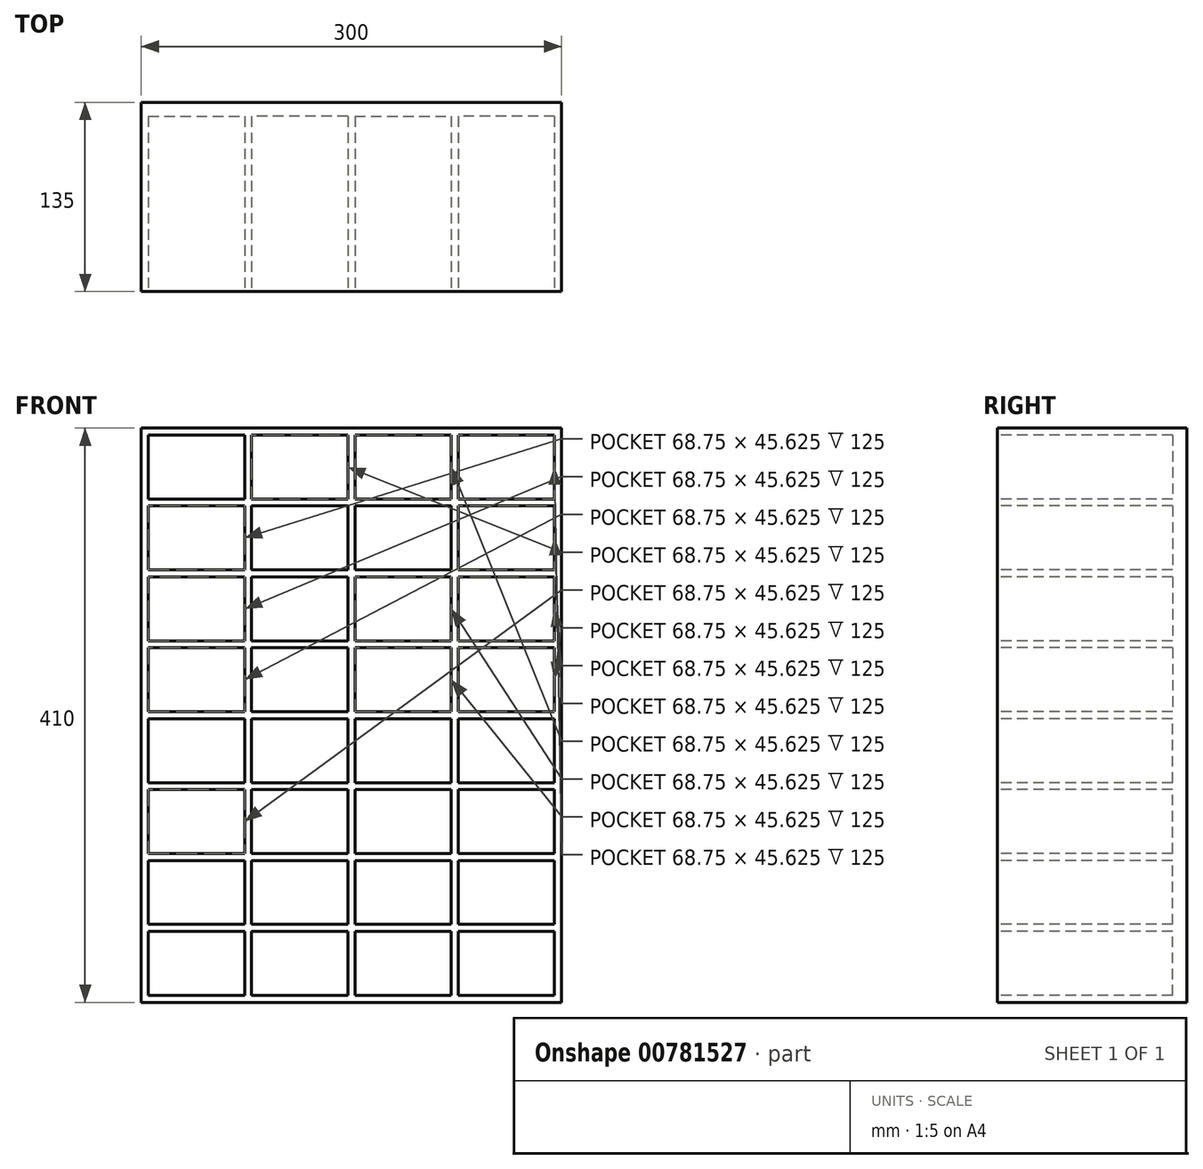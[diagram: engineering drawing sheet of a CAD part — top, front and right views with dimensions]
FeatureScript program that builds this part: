
annotation { "Feature Type Name" : "Feature", "Feature Type Description" : "" }
export const myFeature = defineFeature(function(context is Context, id is Id, definition is map)
    precondition{}
    {
        {
            var Q0;
            Q0=qCreatedBy(makeId("Top.planeOp"),FACE);
            var sketch = newSketch(context, id + "F0", { "sketchPlane" : qUnion([Q0])});
            skLineSegment(sketch, "E0.bottom", {"start": v(0, 0) * mm, "end": v(300, 0) * mm});
            skLineSegment(sketch, "E0.top", {"start": v(0, 135) * mm, "end": v(300, 135) * mm});
            skLineSegment(sketch, "E0.left", {"start": v(0, 0) * mm, "end": v(0, 135) * mm});
            skLineSegment(sketch, "E0.right", {"start": v(300, 0) * mm, "end": v(300, 135) * mm});
            skSolve(sketch);
        }
        {
            var Q0;
            Q0=makeQuery(id+"F0.imprint","IMPRINT",FACE,{"disambiguationData":[TD([[makeQuery(id+"F0.imprint","IMPRINT",EDGE,{"derivedFrom":sQuery(id+"F0.wireOp",EDGE,"E0.bottom")}),1.0]])]});
            extrude(context, id + "F1", {"entities" : qUnion([Q0]), "depth" : 410 * mm, "offsetDistance" : 25 * mm});
        }
        {
            var Q0;
            Q0=makeQuery(id+"F1.opExtrude","SWEPT_FACE",FACE,{"disambiguationData":[OSD([sQuery(id+"F0.wireOp",EDGE,"E0.bottom")])]});
            var sketch = newSketch(context, id + "F2", { "sketchPlane" : qUnion([Q0])});
            skLineSegment(sketch, "E1", {"start": v(0, 205) * mm, "end": v(300, 205) * mm, "construction": true});
            skLineSegment(sketch, "E2.bottom", {"start": v(5, 405) * mm, "end": v(73.75, 405) * mm});
            skLineSegment(sketch, "E2.top", {"start": v(5, 359.38) * mm, "end": v(73.75, 359.38) * mm});
            skLineSegment(sketch, "E2.left", {"start": v(5, 405) * mm, "end": v(5, 359.38) * mm});
            skLineSegment(sketch, "E2.right", {"start": v(73.75, 405) * mm, "end": v(73.75, 359.38) * mm});
            skLineSegment(sketch, "E3.bottom", {"start": v(5, 354.38) * mm, "end": v(73.75, 354.38) * mm});
            skLineSegment(sketch, "E3.top", {"start": v(5, 308.75) * mm, "end": v(73.75, 308.75) * mm});
            skLineSegment(sketch, "E3.left", {"start": v(5, 354.38) * mm, "end": v(5, 308.75) * mm});
            skLineSegment(sketch, "E3.right", {"start": v(73.75, 354.38) * mm, "end": v(73.75, 308.75) * mm});
            skLineSegment(sketch, "E4.bottom", {"start": v(5, 303.75) * mm, "end": v(73.75, 303.75) * mm});
            skLineSegment(sketch, "E4.top", {"start": v(5, 258.12) * mm, "end": v(73.75, 258.12) * mm});
            skLineSegment(sketch, "E4.left", {"start": v(5, 303.75) * mm, "end": v(5, 258.12) * mm});
            skLineSegment(sketch, "E4.right", {"start": v(73.75, 303.75) * mm, "end": v(73.75, 258.13) * mm});
            skLineSegment(sketch, "E5", {"start": v(0, 405) * mm, "end": v(5, 405) * mm});
            skLineSegment(sketch, "E6", {"start": v(5, 359.38) * mm, "end": v(5, 354.38) * mm});
            skLineSegment(sketch, "E7", {"start": v(5, 308.75) * mm, "end": v(5, 303.75) * mm});
            skLineSegment(sketch, "E8.bottom", {"start": v(5, 253.13) * mm, "end": v(73.75, 253.13) * mm});
            skLineSegment(sketch, "E8.top", {"start": v(5, 207.5) * mm, "end": v(73.75, 207.5) * mm});
            skLineSegment(sketch, "E8.left", {"start": v(5, 253.13) * mm, "end": v(5, 207.5) * mm});
            skLineSegment(sketch, "E8.right", {"start": v(73.75, 253.13) * mm, "end": v(73.75, 207.5) * mm});
            skLineSegment(sketch, "E9", {"start": v(5, 258.12) * mm, "end": v(5, 253.13) * mm});
            skLineSegment(sketch, "E10", {"start": v(5, 405) * mm, "end": v(5, 410) * mm});
            skLineSegment(sketch, "E11", {"start": v(76.25, 410) * mm, "end": v(76.25, 205) * mm, "construction": true});
            skLineSegment(sketch, "E12", {"start": v(150, 410) * mm, "end": v(150, 205) * mm, "construction": true});
            skLineSegment(sketch, "E13.MirrorCS", {"start": v(147.5, 405) * mm, "end": v(78.75, 405) * mm});
            skLineSegment(sketch, "E14.MirrorCS", {"start": v(147.5, 405) * mm, "end": v(147.5, 359.38) * mm});
            skLineSegment(sketch, "E15.MirrorCS", {"start": v(78.75, 405) * mm, "end": v(78.75, 359.38) * mm});
            skLineSegment(sketch, "E16.MirrorCS", {"start": v(147.5, 354.38) * mm, "end": v(78.75, 354.38) * mm});
            skLineSegment(sketch, "E17.MirrorCS", {"start": v(78.75, 354.38) * mm, "end": v(78.75, 308.75) * mm});
            skLineSegment(sketch, "E18.MirrorCS", {"start": v(147.5, 359.38) * mm, "end": v(78.75, 359.38) * mm});
            skLineSegment(sketch, "E19.MirrorCS", {"start": v(147.5, 354.38) * mm, "end": v(147.5, 308.75) * mm});
            skLineSegment(sketch, "E20.MirrorCS", {"start": v(147.5, 308.75) * mm, "end": v(78.75, 308.75) * mm});
            skLineSegment(sketch, "E21.MirrorCS", {"start": v(147.5, 303.75) * mm, "end": v(78.75, 303.75) * mm});
            skLineSegment(sketch, "E22.MirrorCS", {"start": v(78.75, 303.75) * mm, "end": v(78.75, 258.13) * mm});
            skLineSegment(sketch, "E23.MirrorCS", {"start": v(147.5, 258.13) * mm, "end": v(78.75, 258.13) * mm});
            skLineSegment(sketch, "E24.MirrorCS", {"start": v(147.5, 303.75) * mm, "end": v(147.5, 258.12) * mm});
            skLineSegment(sketch, "E25.MirrorCS", {"start": v(147.5, 253.13) * mm, "end": v(78.75, 253.13) * mm});
            skLineSegment(sketch, "E26.MirrorCS", {"start": v(78.75, 253.13) * mm, "end": v(78.75, 207.5) * mm});
            skLineSegment(sketch, "E27.MirrorCS", {"start": v(147.5, 207.5) * mm, "end": v(78.75, 207.5) * mm});
            skLineSegment(sketch, "E28.MirrorCS", {"start": v(147.5, 253.13) * mm, "end": v(147.5, 207.5) * mm});
            skLineSegment(sketch, "E29", {"start": v(73.75, 405) * mm, "end": v(78.75, 405) * mm});
            skLineSegment(sketch, "E30.MirrorCS", {"start": v(221.25, 354.38) * mm, "end": v(221.25, 308.75) * mm});
            skLineSegment(sketch, "E31.MirrorCS", {"start": v(152.5, 405) * mm, "end": v(152.5, 359.38) * mm});
            skLineSegment(sketch, "E32.MirrorCS", {"start": v(221.25, 303.75) * mm, "end": v(221.25, 258.13) * mm});
            skLineSegment(sketch, "E33.MirrorCS", {"start": v(152.5, 354.38) * mm, "end": v(152.5, 308.75) * mm});
            skLineSegment(sketch, "E34.MirrorCS", {"start": v(152.5, 253.13) * mm, "end": v(152.5, 207.5) * mm});
            skLineSegment(sketch, "E35.MirrorCS", {"start": v(221.25, 253.13) * mm, "end": v(221.25, 207.5) * mm});
            skLineSegment(sketch, "E36.MirrorCS", {"start": v(152.5, 303.75) * mm, "end": v(152.5, 258.12) * mm});
            skLineSegment(sketch, "E37.MirrorCS", {"start": v(221.25, 405) * mm, "end": v(221.25, 359.38) * mm});
            skLineSegment(sketch, "E38.MirrorCS", {"start": v(152.5, 303.75) * mm, "end": v(221.25, 303.75) * mm});
            skLineSegment(sketch, "E39.MirrorCS", {"start": v(152.5, 258.13) * mm, "end": v(221.25, 258.13) * mm});
            skLineSegment(sketch, "E40.MirrorCS", {"start": v(152.5, 354.38) * mm, "end": v(221.25, 354.38) * mm});
            skLineSegment(sketch, "E41.MirrorCS", {"start": v(152.5, 207.5) * mm, "end": v(221.25, 207.5) * mm});
            skLineSegment(sketch, "E42.MirrorCS", {"start": v(152.5, 359.38) * mm, "end": v(221.25, 359.38) * mm});
            skLineSegment(sketch, "E43.MirrorCS", {"start": v(152.5, 308.75) * mm, "end": v(221.25, 308.75) * mm});
            skLineSegment(sketch, "E44.MirrorCS", {"start": v(152.5, 253.13) * mm, "end": v(221.25, 253.13) * mm});
            skLineSegment(sketch, "E45.MirrorCS", {"start": v(152.5, 405) * mm, "end": v(221.25, 405) * mm});
            skLineSegment(sketch, "E46.MirrorCS", {"start": v(226.25, 405) * mm, "end": v(221.25, 405) * mm});
            skLineSegment(sketch, "E47.MirrorCS", {"start": v(295, 405) * mm, "end": v(295, 359.38) * mm});
            skLineSegment(sketch, "E48.MirrorCS", {"start": v(295, 354.38) * mm, "end": v(295, 308.75) * mm});
            skLineSegment(sketch, "E49.MirrorCS", {"start": v(295, 303.75) * mm, "end": v(295, 258.12) * mm});
            skLineSegment(sketch, "E50.MirrorCS", {"start": v(226.25, 405) * mm, "end": v(226.25, 359.38) * mm});
            skLineSegment(sketch, "E51.MirrorCS", {"start": v(226.25, 354.38) * mm, "end": v(226.25, 308.75) * mm});
            skLineSegment(sketch, "E52.MirrorCS", {"start": v(226.25, 303.75) * mm, "end": v(226.25, 258.13) * mm});
            skLineSegment(sketch, "E53.MirrorCS", {"start": v(226.25, 253.13) * mm, "end": v(226.25, 207.5) * mm});
            skLineSegment(sketch, "E54.MirrorCS", {"start": v(295, 253.13) * mm, "end": v(295, 207.5) * mm});
            skLineSegment(sketch, "E55.MirrorCS", {"start": v(295, 359.38) * mm, "end": v(295, 354.38) * mm});
            skLineSegment(sketch, "E56.MirrorCS", {"start": v(295, 253.13) * mm, "end": v(226.25, 253.13) * mm});
            skLineSegment(sketch, "E57.MirrorCS", {"start": v(295, 258.12) * mm, "end": v(295, 253.13) * mm});
            skLineSegment(sketch, "E58.MirrorCS", {"start": v(295, 354.38) * mm, "end": v(226.25, 354.38) * mm});
            skLineSegment(sketch, "E59.MirrorCS", {"start": v(295, 308.75) * mm, "end": v(295, 303.75) * mm});
            skLineSegment(sketch, "E60.MirrorCS", {"start": v(295, 308.75) * mm, "end": v(226.25, 308.75) * mm});
            skLineSegment(sketch, "E61.MirrorCS", {"start": v(295, 405) * mm, "end": v(226.25, 405) * mm});
            skLineSegment(sketch, "E62.MirrorCS", {"start": v(295, 359.38) * mm, "end": v(226.25, 359.38) * mm});
            skLineSegment(sketch, "E63.MirrorCS", {"start": v(295, 258.13) * mm, "end": v(226.25, 258.13) * mm});
            skLineSegment(sketch, "E64.MirrorCS", {"start": v(295, 303.75) * mm, "end": v(226.25, 303.75) * mm});
            skLineSegment(sketch, "E65.MirrorCS", {"start": v(295, 207.5) * mm, "end": v(226.25, 207.5) * mm});
            skLineSegment(sketch, "E66", {"start": v(147.5, 405) * mm, "end": v(152.5, 405) * mm});
            skLineSegment(sketch, "E67.MirrorCS", {"start": v(73.75, 106.25) * mm, "end": v(73.75, 151.87) * mm});
            skLineSegment(sketch, "E68.MirrorCS", {"start": v(147.5, 5) * mm, "end": v(147.5, 50.62) * mm});
            skLineSegment(sketch, "E69.MirrorCS", {"start": v(147.5, 5) * mm, "end": v(152.5, 5) * mm});
            skLineSegment(sketch, "E70.MirrorCS", {"start": v(221.25, 55.62) * mm, "end": v(221.25, 101.25) * mm});
            skLineSegment(sketch, "E71.MirrorCS", {"start": v(5, 106.25) * mm, "end": v(73.75, 106.25) * mm});
            skLineSegment(sketch, "E72.MirrorCS", {"start": v(73.75, 5) * mm, "end": v(73.75, 50.62) * mm});
            skLineSegment(sketch, "E73.MirrorCS", {"start": v(295, 101.25) * mm, "end": v(226.25, 101.25) * mm});
            skLineSegment(sketch, "E74.MirrorCS", {"start": v(73.75, 156.87) * mm, "end": v(73.75, 202.5) * mm});
            skLineSegment(sketch, "E75.MirrorCS", {"start": v(295, 50.62) * mm, "end": v(226.25, 50.62) * mm});
            skLineSegment(sketch, "E76.MirrorCS", {"start": v(5, 55.62) * mm, "end": v(5, 101.25) * mm});
            skLineSegment(sketch, "E77.MirrorCS", {"start": v(295, 156.88) * mm, "end": v(295, 202.5) * mm});
            skLineSegment(sketch, "E78.MirrorCS", {"start": v(226.25, 5) * mm, "end": v(221.25, 5) * mm});
            skLineSegment(sketch, "E79.MirrorCS", {"start": v(152.5, 101.25) * mm, "end": v(221.25, 101.25) * mm});
            skLineSegment(sketch, "E80.MirrorCS", {"start": v(295, 156.87) * mm, "end": v(226.25, 156.87) * mm});
            skLineSegment(sketch, "E81.MirrorCS", {"start": v(147.5, 101.25) * mm, "end": v(78.75, 101.25) * mm});
            skLineSegment(sketch, "E82.MirrorCS", {"start": v(226.25, 106.25) * mm, "end": v(226.25, 151.87) * mm});
            skLineSegment(sketch, "E83.MirrorCS", {"start": v(295, 101.25) * mm, "end": v(295, 106.25) * mm});
            skLineSegment(sketch, "E84.MirrorCS", {"start": v(5, 5) * mm, "end": v(73.75, 5) * mm});
            skLineSegment(sketch, "E85.MirrorCS", {"start": v(226.25, 156.87) * mm, "end": v(226.25, 202.5) * mm});
            skLineSegment(sketch, "E86.MirrorCS", {"start": v(78.75, 55.62) * mm, "end": v(78.75, 101.25) * mm});
            skLineSegment(sketch, "E87.MirrorCS", {"start": v(5, 50.62) * mm, "end": v(73.75, 50.62) * mm});
            skLineSegment(sketch, "E88.MirrorCS", {"start": v(226.25, 55.62) * mm, "end": v(226.25, 101.25) * mm});
            skLineSegment(sketch, "E89.MirrorCS", {"start": v(152.5, 55.62) * mm, "end": v(152.5, 101.25) * mm});
            skLineSegment(sketch, "E90.MirrorCS", {"start": v(147.5, 106.25) * mm, "end": v(78.75, 106.25) * mm});
            skLineSegment(sketch, "E91.MirrorCS", {"start": v(152.5, 151.87) * mm, "end": v(221.25, 151.87) * mm});
            skLineSegment(sketch, "E92.MirrorCS", {"start": v(78.75, 156.87) * mm, "end": v(78.75, 202.5) * mm});
            skLineSegment(sketch, "E93.MirrorCS", {"start": v(295, 106.25) * mm, "end": v(295, 151.88) * mm});
            skLineSegment(sketch, "E94.MirrorCS", {"start": v(147.5, 5) * mm, "end": v(78.75, 5) * mm});
            skLineSegment(sketch, "E95.MirrorCS", {"start": v(152.5, 50.62) * mm, "end": v(221.25, 50.62) * mm});
            skLineSegment(sketch, "E96.MirrorCS", {"start": v(295, 5) * mm, "end": v(295, 50.62) * mm});
            skLineSegment(sketch, "E97.MirrorCS", {"start": v(5, 156.88) * mm, "end": v(5, 202.5) * mm});
            skLineSegment(sketch, "E98.MirrorCS", {"start": v(147.5, 151.87) * mm, "end": v(78.75, 151.87) * mm});
            skLineSegment(sketch, "E99.MirrorCS", {"start": v(5, 106.25) * mm, "end": v(5, 151.88) * mm});
            skLineSegment(sketch, "E100.MirrorCS", {"start": v(147.5, 202.5) * mm, "end": v(78.75, 202.5) * mm});
            skLineSegment(sketch, "E101.MirrorCS", {"start": v(5, 151.87) * mm, "end": v(73.75, 151.87) * mm});
            skLineSegment(sketch, "E102.MirrorCS", {"start": v(78.75, 106.25) * mm, "end": v(78.75, 151.87) * mm});
            skLineSegment(sketch, "E103.MirrorCS", {"start": v(221.25, 5) * mm, "end": v(221.25, 50.62) * mm});
            skLineSegment(sketch, "E104.MirrorCS", {"start": v(5, 101.25) * mm, "end": v(5, 106.25) * mm});
            skLineSegment(sketch, "E105.MirrorCS", {"start": v(5, 202.5) * mm, "end": v(73.75, 202.5) * mm});
            skLineSegment(sketch, "E106.MirrorCS", {"start": v(5, 50.62) * mm, "end": v(5, 55.62) * mm});
            skLineSegment(sketch, "E107.MirrorCS", {"start": v(5, 5) * mm, "end": v(5, 50.62) * mm});
            skLineSegment(sketch, "E108.MirrorCS", {"start": v(5, 156.87) * mm, "end": v(73.75, 156.87) * mm});
            skLineSegment(sketch, "E109.MirrorCS", {"start": v(295, 55.62) * mm, "end": v(226.25, 55.62) * mm});
            skLineSegment(sketch, "E110.MirrorCS", {"start": v(73.75, 55.62) * mm, "end": v(73.75, 101.25) * mm});
            skLineSegment(sketch, "E111.MirrorCS", {"start": v(152.5, 106.25) * mm, "end": v(221.25, 106.25) * mm});
            skLineSegment(sketch, "E112.MirrorCS", {"start": v(152.5, 106.25) * mm, "end": v(152.5, 151.88) * mm});
            skLineSegment(sketch, "E113.MirrorCS", {"start": v(295, 55.62) * mm, "end": v(295, 101.25) * mm});
            skLineSegment(sketch, "E114.MirrorCS", {"start": v(295, 5) * mm, "end": v(226.25, 5) * mm});
            skLineSegment(sketch, "E115.MirrorCS", {"start": v(5, 101.25) * mm, "end": v(73.75, 101.25) * mm});
            skLineSegment(sketch, "E116.MirrorCS", {"start": v(5, 55.62) * mm, "end": v(73.75, 55.62) * mm});
            skLineSegment(sketch, "E117.MirrorCS", {"start": v(147.5, 55.62) * mm, "end": v(147.5, 101.25) * mm});
            skLineSegment(sketch, "E118.MirrorCS", {"start": v(295, 202.5) * mm, "end": v(226.25, 202.5) * mm});
            skLineSegment(sketch, "E119.MirrorCS", {"start": v(221.25, 156.87) * mm, "end": v(221.25, 202.5) * mm});
            skLineSegment(sketch, "E120.MirrorCS", {"start": v(147.5, 55.62) * mm, "end": v(78.75, 55.62) * mm});
            skLineSegment(sketch, "E121.MirrorCS", {"start": v(152.5, 5) * mm, "end": v(152.5, 50.62) * mm});
            skLineSegment(sketch, "E122.MirrorCS", {"start": v(73.75, 5) * mm, "end": v(78.75, 5) * mm});
            skLineSegment(sketch, "E123.MirrorCS", {"start": v(152.5, 202.5) * mm, "end": v(221.25, 202.5) * mm});
            skLineSegment(sketch, "E124.MirrorCS", {"start": v(221.25, 106.25) * mm, "end": v(221.25, 151.87) * mm});
            skLineSegment(sketch, "E125.MirrorCS", {"start": v(295, 151.88) * mm, "end": v(295, 156.88) * mm});
            skLineSegment(sketch, "E126.MirrorCS", {"start": v(152.5, 5) * mm, "end": v(221.25, 5) * mm});
            skLineSegment(sketch, "E127.MirrorCS", {"start": v(78.75, 5) * mm, "end": v(78.75, 50.62) * mm});
            skLineSegment(sketch, "E128.MirrorCS", {"start": v(147.5, 50.62) * mm, "end": v(78.75, 50.62) * mm});
            skLineSegment(sketch, "E129.MirrorCS", {"start": v(147.5, 156.88) * mm, "end": v(147.5, 202.5) * mm});
            skLineSegment(sketch, "E130.MirrorCS", {"start": v(152.5, 156.87) * mm, "end": v(221.25, 156.87) * mm});
            skLineSegment(sketch, "E131.MirrorCS", {"start": v(295, 50.62) * mm, "end": v(295, 55.62) * mm});
            skLineSegment(sketch, "E132.MirrorCS", {"start": v(147.5, 106.25) * mm, "end": v(147.5, 151.88) * mm});
            skLineSegment(sketch, "E133.MirrorCS", {"start": v(295, 151.87) * mm, "end": v(226.25, 151.87) * mm});
            skLineSegment(sketch, "E134.MirrorCS", {"start": v(152.5, 55.62) * mm, "end": v(221.25, 55.62) * mm});
            skLineSegment(sketch, "E135.MirrorCS", {"start": v(226.25, 5) * mm, "end": v(226.25, 50.62) * mm});
            skLineSegment(sketch, "E136.MirrorCS", {"start": v(152.5, 156.88) * mm, "end": v(152.5, 202.5) * mm});
            skLineSegment(sketch, "E137.MirrorCS", {"start": v(147.5, 156.87) * mm, "end": v(78.75, 156.87) * mm});
            skLineSegment(sketch, "E138.MirrorCS", {"start": v(5, 151.88) * mm, "end": v(5, 156.88) * mm});
            skLineSegment(sketch, "E139.MirrorCS", {"start": v(295, 106.25) * mm, "end": v(226.25, 106.25) * mm});
            skLineSegment(sketch, "E140", {"start": v(5, 202.5) * mm, "end": v(5, 207.5) * mm});
            skSolve(sketch);
        }
        {
            var Q0;
            Q0=qSketchRegion(id+"F2",true);
            extrude(context, id + "F3", {"entities" : qUnion([Q0]), "operationType" : NewBodyOperationType.REMOVE, "oppositeDirection" : true, "depth" : 125 * mm, "offsetDistance" : 25 * mm});
        }
    });
